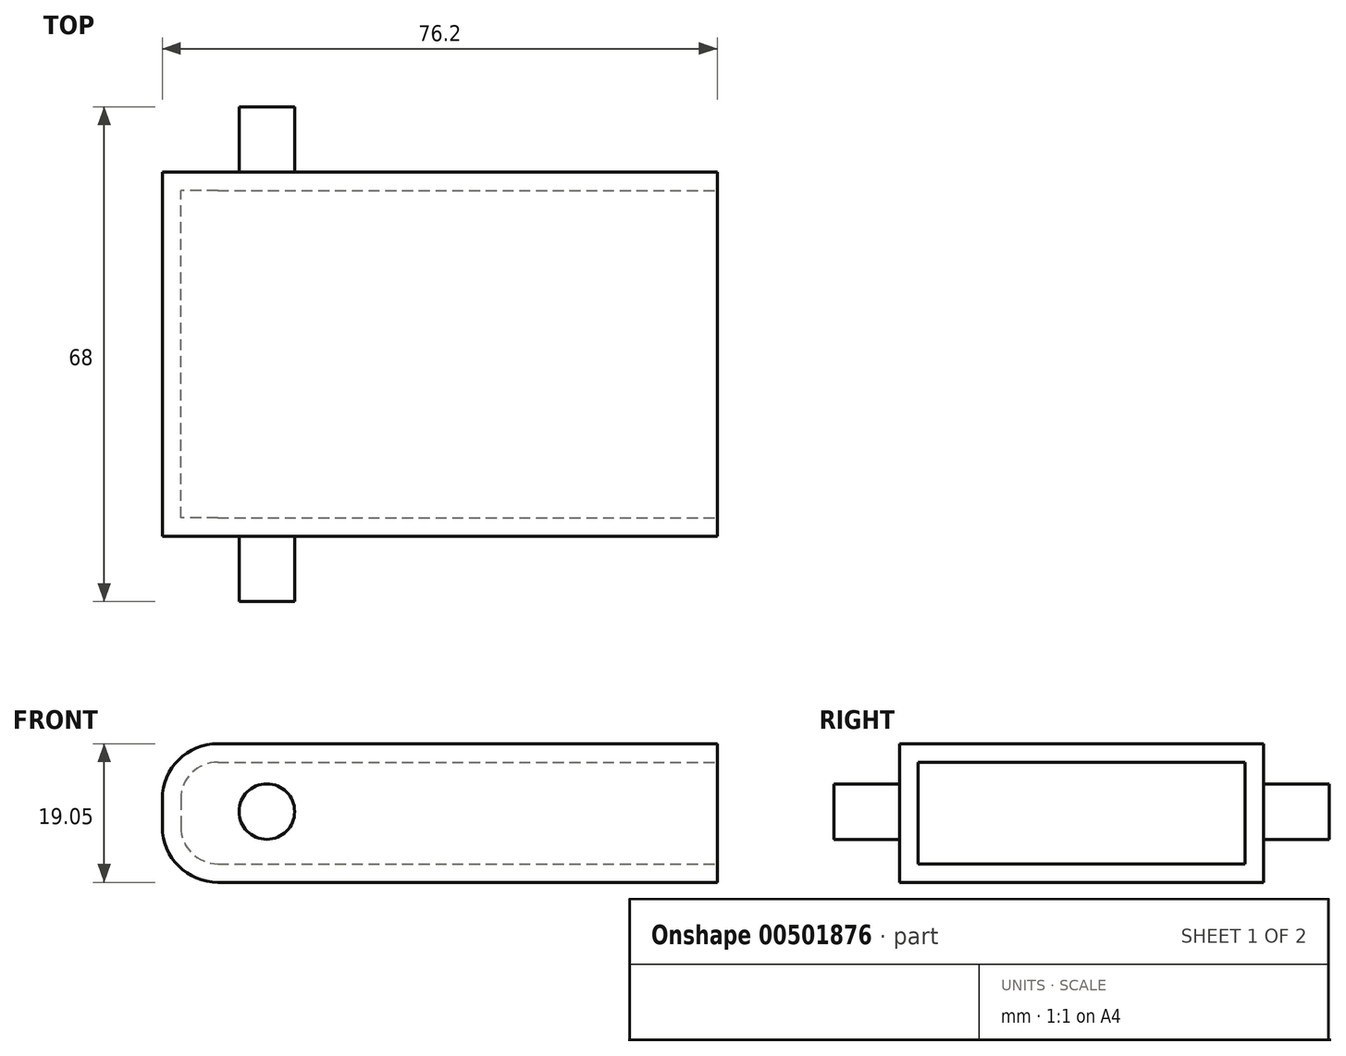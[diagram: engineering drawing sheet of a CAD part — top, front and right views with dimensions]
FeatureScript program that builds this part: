
annotation { "Feature Type Name" : "Feature", "Feature Type Description" : "" }
export const myFeature = defineFeature(function(context is Context, id is Id, definition is map)
    precondition{}
    {
        {
            var Q0;
            Q0=qCreatedBy(makeId("Front.planeOp"),FACE);
            var sketch = newSketch(context, id + "F0", { "sketchPlane" : qUnion([Q0])});
            skLineSegment(sketch, "E0.bottom", {"start": v(-37.21, 9.34) * mm, "end": v(31.37, 9.34) * mm});
            skLineSegment(sketch, "E0.top", {"start": v(-37.21, -9.7) * mm, "end": v(31.37, -9.7) * mm});
            skLineSegment(sketch, "E0.left", {"start": v(-44.83, 1.72) * mm, "end": v(-44.83, -2.09) * mm});
            skLineSegment(sketch, "E0.right", {"start": v(31.37, 9.34) * mm, "end": v(31.37, -9.7) * mm});
            skPoint(sketch, "E1.visualSharp", {"position": v(-44.83, 9.34) * mm});
            skArc(sketch, "E1.filletArc", {"start": v(-37.21, 9.34) * mm, "mid": v(-42.6, 7.1) * mm, "end": v(-44.83, 1.72) * mm});
            skPoint(sketch, "E2.visualSharp", {"position": v(-44.83, -9.7) * mm});
            skArc(sketch, "E2.filletArc", {"start": v(-44.83, -2.09) * mm, "mid": v(-42.6, -7.48) * mm, "end": v(-37.21, -9.7) * mm});
            skSolve(sketch);
        }
        {
            var Q0;
            Q0=makeQuery(id+"F0.imprint","IMPRINT",FACE,{"disambiguationData":[TD([[makeQuery(id+"F0.imprint","IMPRINT",EDGE,{"derivedFrom":sQuery(id+"F0.wireOp",EDGE,"E0.bottom")}),-1.0]])]});
            extrude(context, id + "F1", {"entities" : qUnion([Q0]), "depth" : 50 * mm});
        }
        {
            var Q0;
            Q0=makeQuery(id+"F1.opExtrude","SWEPT_FACE",FACE,{"disambiguationData":[OSD([sQuery(id+"F0.wireOp",EDGE,"E0.right")])]});
            shell(context, id + "F2", {"entities" : qUnion([Q0]), "thickness" : 2.54 * mm});
        }
        {
            var Q0;
            Q0=makeQuery(id+"F1.opExtrude","CAP_FACE",FACE,{"disambiguationData":[OSD([sQuery(id+"F0.wireOp",EDGE,"E0.bottom"),sQuery(id+"F0.wireOp",EDGE,"E0.top"),sQuery(id+"F0.wireOp",EDGE,"E0.left"),sQuery(id+"F0.wireOp",EDGE,"E0.right"),sQuery(id+"F0.wireOp",EDGE,"E1.filletArc"),sQuery(id+"F0.wireOp",EDGE,"E2.filletArc")])],"isStart":false});
            var sketch = newSketch(context, id + "F3", { "sketchPlane" : qUnion([Q0])});
            skCircle(sketch, "E3", {"center": v(-30.48, 0) * mm, "radius": 3.81 * mm});
            skSolve(sketch);
        }
        {
            var Q0;
            Q0 = qSketchRegion(id + "F3", true);
            extrude(context, id + "F4", {"entities" : qUnion([Q0]), "operationType" : NewBodyOperationType.ADD, "depth" : 9 * mm});
        }
        {
            var Q0;
            Q0=makeQuery(id+"F1.opExtrude","CAP_FACE",FACE,{"disambiguationData":[OSD([sQuery(id+"F0.wireOp",EDGE,"E0.bottom"),sQuery(id+"F0.wireOp",EDGE,"E0.top"),sQuery(id+"F0.wireOp",EDGE,"E0.left"),sQuery(id+"F0.wireOp",EDGE,"E0.right"),sQuery(id+"F0.wireOp",EDGE,"E1.filletArc"),sQuery(id+"F0.wireOp",EDGE,"E2.filletArc")])],"isStart":true});
            var sketch = newSketch(context, id + "F5", { "sketchPlane" : qUnion([Q0])});
            skCircle(sketch, "E4", {"center": v(30.48, 0) * mm, "radius": 3.81 * mm});
            skSolve(sketch);
        }
        {
            var Q0;
            Q0=makeQuery(id+"F5.imprint","IMPRINT",FACE,{"disambiguationData":[TD([[makeQuery(id+"F5.imprint","IMPRINT",EDGE,{"derivedFrom":sQuery(id+"F5.wireOp",EDGE,"E4")}),1.0]])]});
            extrude(context, id + "F6", {"entities" : qUnion([Q0]), "operationType" : NewBodyOperationType.ADD, "depth" : 9 * mm});
        }
    });
